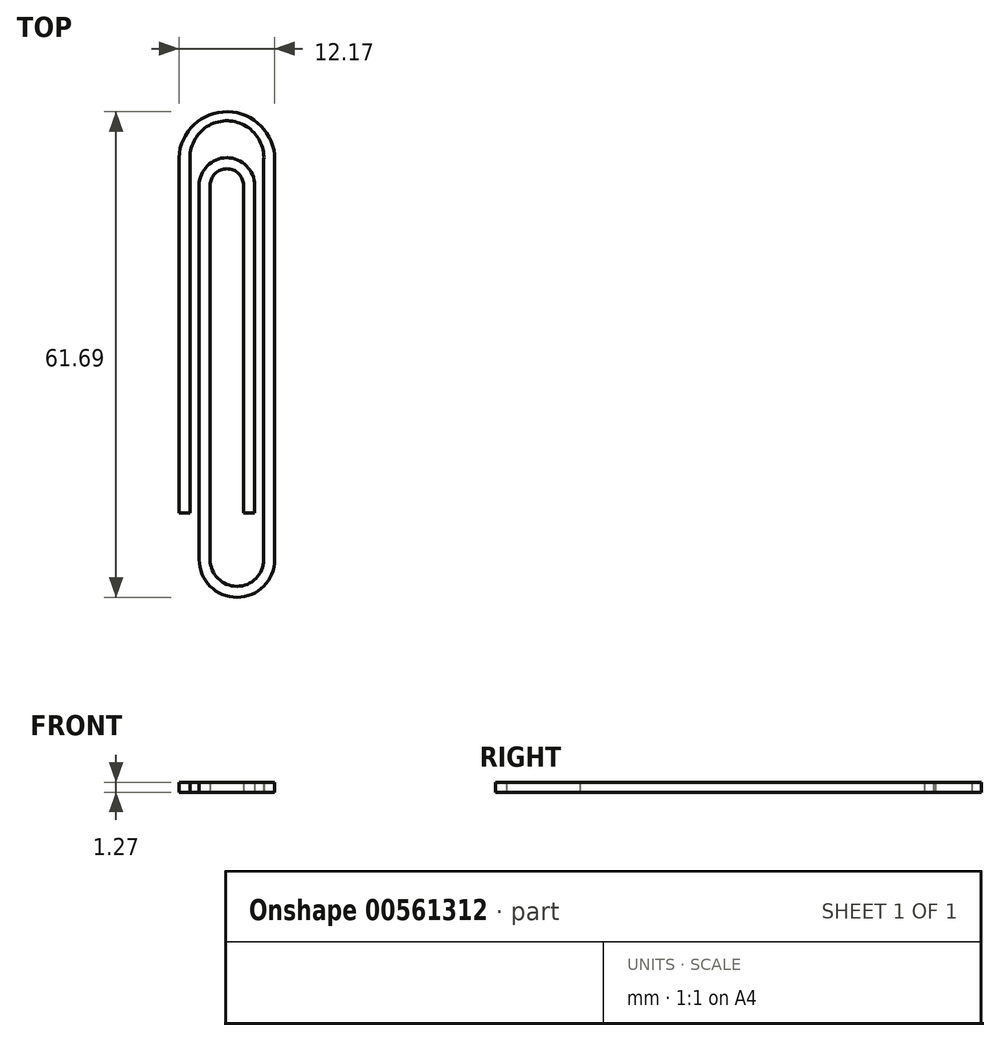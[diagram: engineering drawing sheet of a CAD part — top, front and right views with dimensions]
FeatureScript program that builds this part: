
annotation { "Feature Type Name" : "Feature", "Feature Type Description" : "" }
export const myFeature = defineFeature(function(context is Context, id is Id, definition is map)
    precondition{}
    {
        {
            var Q0;
            Q0=qCreatedBy(makeId("Top.planeOp"),FACE);
            var sketch = newSketch(context, id + "F0", { "sketchPlane" : qUnion([Q0])});
            skLineSegment(sketch, "E0", {"start": v(-3.66, -23.47) * mm, "end": v(-3.66, 27.33) * mm});
            skLineSegment(sketch, "E1", {"start": v(-3.66, 27.33) * mm, "end": v(-2.27, 27.33) * mm});
            skLineSegment(sketch, "E2", {"start": v(-2.27, 27.33) * mm, "end": v(-2.27, -23.47) * mm});
            skArc(sketch, "E3", {"start": v(-10.47, -23.47) * mm, "mid": v(-7.07, -26.88) * mm, "end": v(-3.66, -23.47) * mm});
            skArc(sketch, "E4", {"start": v(-11.87, -23.47) * mm, "mid": v(-7.07, -28.27) * mm, "end": v(-2.27, -23.47) * mm});
            skLineSegment(sketch, "E5", {"start": v(-10.47, -23.47) * mm, "end": v(-10.47, 24.05) * mm});
            skLineSegment(sketch, "E6", {"start": v(-11.87, -23.47) * mm, "end": v(-11.87, 24.05) * mm});
            skPoint(sketch, "E7.endSnap0", {"position": v(-2.96, 27.33) * mm});
            skLineSegment(sketch, "E8", {"start": v(-4.83, 24.05) * mm, "end": v(-4.83, -23.47) * mm});
            skLineSegment(sketch, "E9", {"start": v(-6.23, 24.05) * mm, "end": v(-6.23, -23.47) * mm});
            skArc(sketch, "E10", {"start": v(-6.23, 24.05) * mm, "mid": v(-8.35, 26.17) * mm, "end": v(-10.47, 24.05) * mm});
            skArc(sketch, "E11", {"start": v(-4.83, 24.05) * mm, "mid": v(-8.35, 27.57) * mm, "end": v(-11.87, 24.05) * mm});
            skLineSegment(sketch, "E12", {"start": v(-13.04, 24.05) * mm, "end": v(-13.04, -23.74) * mm});
            skLineSegment(sketch, "E13", {"start": v(-13.04, 24.05) * mm, "end": v(-13.04, 27.57) * mm});
            skPoint(sketch, "E13.endSnap0", {"position": v(-8.35, 27.57) * mm});
            skLineSegment(sketch, "E14", {"start": v(-13.04, 27.57) * mm, "end": v(-14.44, 27.57) * mm});
            skLineSegment(sketch, "E15", {"start": v(-14.44, 27.57) * mm, "end": v(-14.44, -23.74) * mm});
            skLineSegment(sketch, "E16", {"start": v(-14.44, -23.74) * mm, "end": v(-13.04, -23.74) * mm});
            skArc(sketch, "E17", {"start": v(-3.66, 27.33) * mm, "mid": v(-8.23, 32.26) * mm, "end": v(-13.04, 27.57) * mm});
            skArc(sketch, "E18", {"start": v(-2.27, 27.33) * mm, "mid": v(-8.23, 33.42) * mm, "end": v(-14.44, 27.57) * mm});
            skLineSegment(sketch, "E19", {"start": v(-6.23, -23.47) * mm, "end": v(-4.83, -23.47) * mm});
            skLineSegment(sketch, "E20", {"start": v(-13.04, -17.56) * mm, "end": v(-14.44, -17.56) * mm});
            skLineSegment(sketch, "E21", {"start": v(-6.23, -17.56) * mm, "end": v(-4.83, -17.56) * mm});
            skPoint(sketch, "E22", {"position": v(-8.47, 33.42) * mm});
            skPoint(sketch, "E22.positionSnap0", {"position": v(-8.23, 33.42) * mm});
            skPoint(sketch, "E23", {"position": v(-6.92, -28.27) * mm});
            skSolve(sketch);
        }
        {
            var Q0;
            {var subQ3=sQuery(id+"F0.wireOp",EDGE,"E13");Q0=makeQuery(id+"F0.imprint","IMPRINT",FACE,{"disambiguationData":[TD([[makeQuery(id+"F0.imprint","IMPRINT",EDGE,{"derivedFrom":subQ3}),1.0]])]});}
            var Q1;
            Q1=makeQuery(id+"F0.imprint","IMPRINT",FACE,{"disambiguationData":[TD([[makeQuery(id+"F0.imprint","IMPRINT",EDGE,{"derivedFrom":sQuery(id+"F0.wireOp",EDGE,"E0")}),-1.0]])]});
            var Q2;
            Q2=makeQuery(id+"F0.imprint","IMPRINT",FACE,{"disambiguationData":[TD([[makeQuery(id+"F0.imprint","IMPRINT",EDGE,{"derivedFrom":sQuery(id+"F0.wireOp",EDGE,"E1")}),1.0]])]});
            extrude(context, id + "F1", {"entities" : qUnion([Q0, Q1, Q2]), "depth" : 1.27 * mm, "offsetDistance" : 25.4 * mm});
        }
    });
